# Revit family: 90926
name_source: partatom
category: Aparatos sanitarios
revit_build: Autodesk Revit 2017 (Build: 20160225_1515(x64)
units: mm (PartAtom-declared; Revit-internal decimal feet)

## family parameters
Anfitrión = Cara
Compartido = No
Corte con vacíos al cargar = No
Cota de conector redondo = Diámetro de uso
Número OmniClass = 23.45.55.14
Punto de cálculo de habitación = No
Tipo de pieza = Normal
Título OmniClass = Single Faucets

## types (1)
- 90926
    Accionamiento = Mediante pulsador
    CAUDAL = 5 l/min
5 l/min
    CIERRE = Automático en 10 seg.
    Comentarios de tipo = Cuerpo en pintura de alta resistencia y pulsador en latón cromado. Piezas interiores en matieriales resistentes a la corrosión e incrustaciones calcáreas. Cabeza intercambiable.Suministrado con brida, latiguillos flexibles en acero inoxidable de  1/2" y 350 mm, 2 llaves de paso y juntas. Válvulas antirretorno incorporadas que impiden la intercomunicación de agua fría y caliente. Selección de temperatura por maneta lateral.
    Conexión AC = Sí
    Conexión AF = Sí
    Código de montaje = C1030220
    Descripción = Grifos temporalizado mezclador para instalación sobre repisa y apertura por pulsador.
    ENTRADA = Con latiguillos flexibles de 1/2"
    Elevación por defecto = 1219 mm
    Fabricante = PRESTO IBÉRICA
    Imagen de tipo = <Ninguno>
    Material = LATON CROMADO
    Modelo = PRESTO XT 2000 - LM Negro
    PESO BRUTO = 1,320 Kg
    Presión Máxima = Max. 8 bar
    REFERENCIA = 90926
    TIPO DE AGUA = Fria/Caliente
    Teléfono = (+34) 915 782 575
    URL = http://www.griferiasgalindo.com
